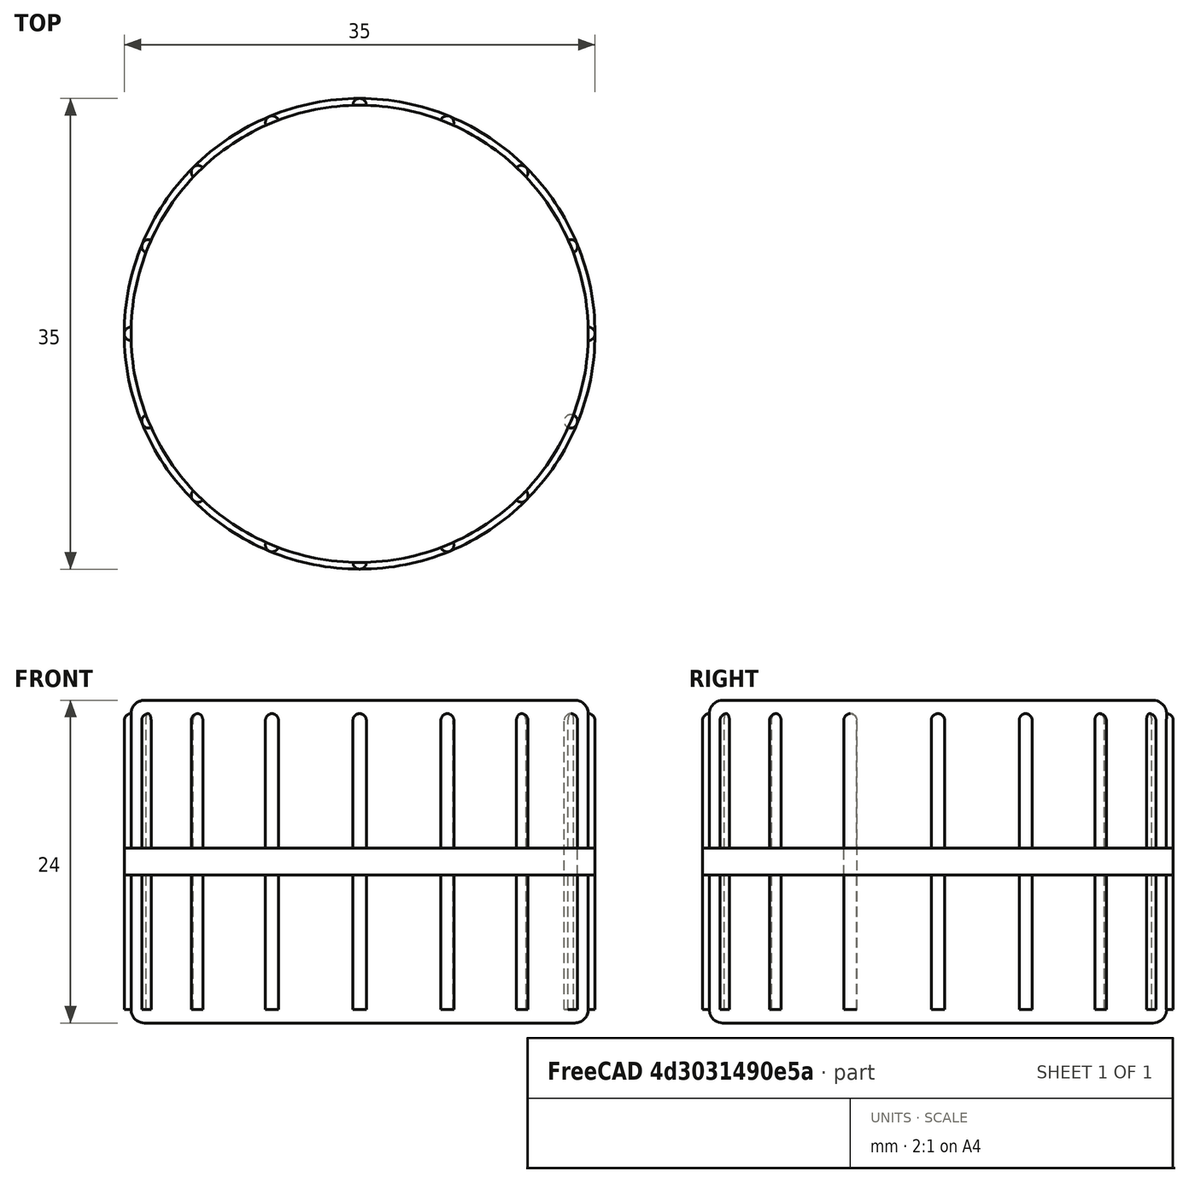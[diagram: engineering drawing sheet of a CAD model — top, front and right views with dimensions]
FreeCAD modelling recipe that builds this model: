
FCSTD DOCUMENT  (FreeCAD 0.16RUnknown)
Label: Acople_mesa
License: All rights reserved
LicenseURL: http://en.wikipedia.org/wiki/All_rights_reserved
objects: Part::Cylinder×3, Part::MultiFuse×2, Part::Fillet×2, Part::FeaturePython×1
note: 8 computed .brp shape members not serialized (recipe doc carries the construction recipe); baked Part::Feature solids carry a one-line shape summary decoded from their .brp

FEATURE [Part::Cylinder] Cylinder  label="Cilindro interno"
  Angle = 360
  Height = 24
  Placement = pos=(0,0,-11) rot=(0,0,1;0rad)
  Radius = 17
FEATURE [Part::Cylinder] Cylinder001  label="Cilindro externo"
  Angle = 360
  Height = 2
  Radius = 17.5
FEATURE [Part::MultiFuse] Fusion  label="Acople mesa"
  Shapes = -> [Cylinder,Cylinder001]
FEATURE [Part::Cylinder] Cylinder003  label="Cylinder"
  Angle = 360
  Height = 22
  Placement = pos=(0,17,-10) rot=(0,0,1;0rad)
  Radius = 0.5
FEATURE [Part::Fillet] Fillet  label="Cilindro con fillet"
  Base = -> Cylinder003
  Edges = 1 edges r=0.5: [Edge1]
FEATURE [Part::Fillet] Fillet001  label="Acople con fillet"
  Base = -> Fusion
  Edges = 2 edges r=1: [Edge1,Edge9]
FEATURE [Part::FeaturePython] Array  label="Cilindros de ajuste"  # Draft array (typed FeaturePython)
  Angle = 360
  ArrayType = 1
  Axis = (0,0,1)
  Base = -> Fillet
  Center = (0,0,0)
  Fuse = false
  IntervalAxis = (0,0,0)
  IntervalX = (1,0,0)
  IntervalY = (0,1,0)
  IntervalZ = (0,0,0)
  NumberPolar = 16
  NumberX = 2
  NumberY = 2
  NumberZ = 1
FEATURE [Part::MultiFuse] Fusion001  label="Prototipo4"
  Shapes = -> [Array,Fillet001]
